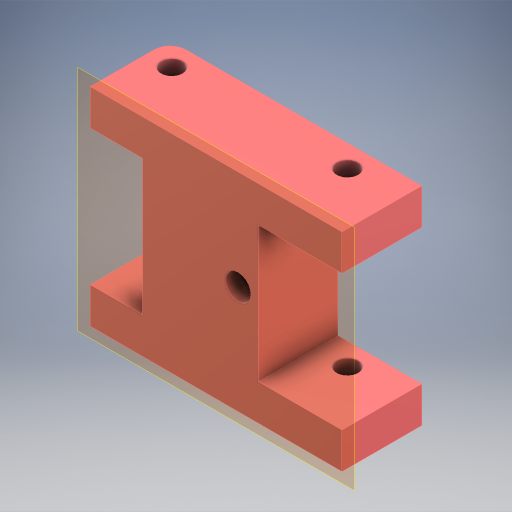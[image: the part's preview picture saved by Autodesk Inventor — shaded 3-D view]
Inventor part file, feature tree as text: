
AUTODESK INVENTOR PART (.ipt)
format: ipt  version: 2024 (Build 280153000, 153)  size: 279,040 bytes
history: native  units: in
note: dims shown in document units (in); Inventor stores cm internally (conversion verified against a paired STEP export)
features: other x4, extrude x2, sketch x2, reference x2, fillet x1
ambient origin geometry x8: Origin, YZ Plane, XZ Plane, XY Plane, X Axis, Y Axis, Z Axis, Center Point
bodies: Body1 (feature_tree)
feature tree (11):
  other  "솔리드1"
  other  "작업 평면4"
  extrude  "돌출1"  Depth=0.3937in TaperAngle=0.0deg
  extrude  "돌출2"  TaperAngle=0.0deg  [1 undecoded]
  fillet  "모깎기1"  Radius=0.0787in
  sketch  "스케치5"
  reference  "참조2"
  sketch  "스케치6"
  reference  "참조3"
  other  "조립품7"
  other  "foot_right_bottom_MIR_MIR:1"
note: 1 required parameter value undecoded (feature->parameter linkage not recoverable at this tier; creation-order binding heuristic only, values carry confidence <= 0.55)
